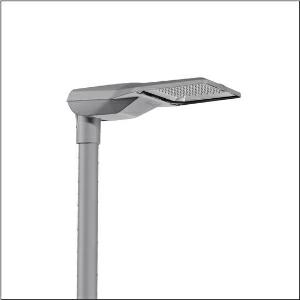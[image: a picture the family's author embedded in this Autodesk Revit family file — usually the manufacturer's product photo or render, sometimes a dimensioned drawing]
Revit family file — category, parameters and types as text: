
# Revit family: streetlight_sl_21_midi___st1_0a_5xe7d33a08lb_7026
name_source: partatom
category: Lighting Fixtures
units: mm (PartAtom-declared; Revit-internal decimal feet)

## family parameters
Cut with Voids When Loaded = No
Host = Face
Light Source = No
Part Type = Normal
Room Calculation Point = No
Round Connector Dimension = Use Diameter
Shared = No

## types (1)
- --- (1 x LED, 14340 lm, 98.3 W, 3000K)
    Apparent Load = 98 VA
    CIE Flux Codes = 37 72 97 100 100
    Color Rendering = 70
    Color Temperature = 3000K
    Default Elevation = 1800 mm
    Description = Streetlight SL 21 midi, mast luminaire, primary light control with lens, of PMMA, primary optical cover: cover, of toughened safety glass, transparent, light distribution: ST1.0a, light emission: direct distribution, primary light characteristic: asymmetric, installation type: post-top, side-entry, LED, 3G 1.5mm², High Power LED, rated luminous flux: 14.340lm, luminous efficacy: 146lm/W, light colour: 730, colour temperature: 3000K, control: flexible luminous flux parameterisation, time-dependent luminous flux control, constant luminous flux control, overheat protection, mains connection: 220..240V, AC, 50/60Hz, connection cable pre-assembled, cable length: 10,5m, wiring characteristics: H07RN-F, start of lifetime: 98W, end of service life: 101W, reduction: 44W, luminaire housing, of diecast aluminium, powder-coated, Siteco® metallic grey (DB 702S), corrosivity category C5 mid according to DIN EN ISO 12944, please order mast flange separately, inclination adjustable: 0°, 5°, 10°, 15°, sealing non-destructively replaceable, multi-level sealing system, length: 644mm, width: 335mm, height: 110mm, mast flange for spigot size: 42mm (side-entry): 5XC10008XM4, 60/48mm (side-entry/post-top): 5XC10108XM2, 76/60mm (side-entry/post-top): 5XC10108XM1, protection rating (complete): IP66, insulation class (complete): insulation class II (safety insulation), certification: CE, ENEC, ENEC+, VDE, impact resistance: IK09, permissible operating ambient temperature for outdoor applications: -40..+50°C, standard-compliant lighting for roads and squares, packaging unit: 1 piece

Light Distribution: ST1.0a
    Height = 111 mm
    Lamp = 1 x LED
    Lamp Light Flux = 14340 lm
    Lamp Power = 98.3 W
    Lamp count = 1
    Length = 644 mm
    Luminous efficacy = 146 lm/W
    Manufacturer = Siteco
    ModVariant = No
    Model = 5XE7D33A08LB
    Number of Poles = 1
    OnlyDefault = Yes
    Power Factor = 1
    Product Name = Streetlight SL 21 midi | ST1.0a
    Product group = mast luminaire | pylon top
    ProductGroupID = 6100
    Protection Class = Protection class II
    Protection Degree = IP 66
    RLX_Detail_Level = 1
    RLX_Emergency_Light_Flux = 0 lm
    RLX_Emergency_Type = 0
    RLX_Emergency_Type_DB = No
    RlxData = <blob elided: 90593 chars, md5=6df86913>
    Socket = socket
    Standby Power = 0 W
    System Light Flux = 14340 lm
    System Power = 98 W
    Type Comments = factory setting: luminous flux: 100 % | Output Level: 100 % | 1020 mA
    Type Image = l_1004298.jpg
    URL = http://relux.com
    VarID = @adj_122875
    Voltage = 0 V
    Weight = 0.00 kg
    Width = 336 mm

## geometry (parser evidence)
native form markers: Blend x4, Sweep x11
no freeform markers — native parametric forms only
